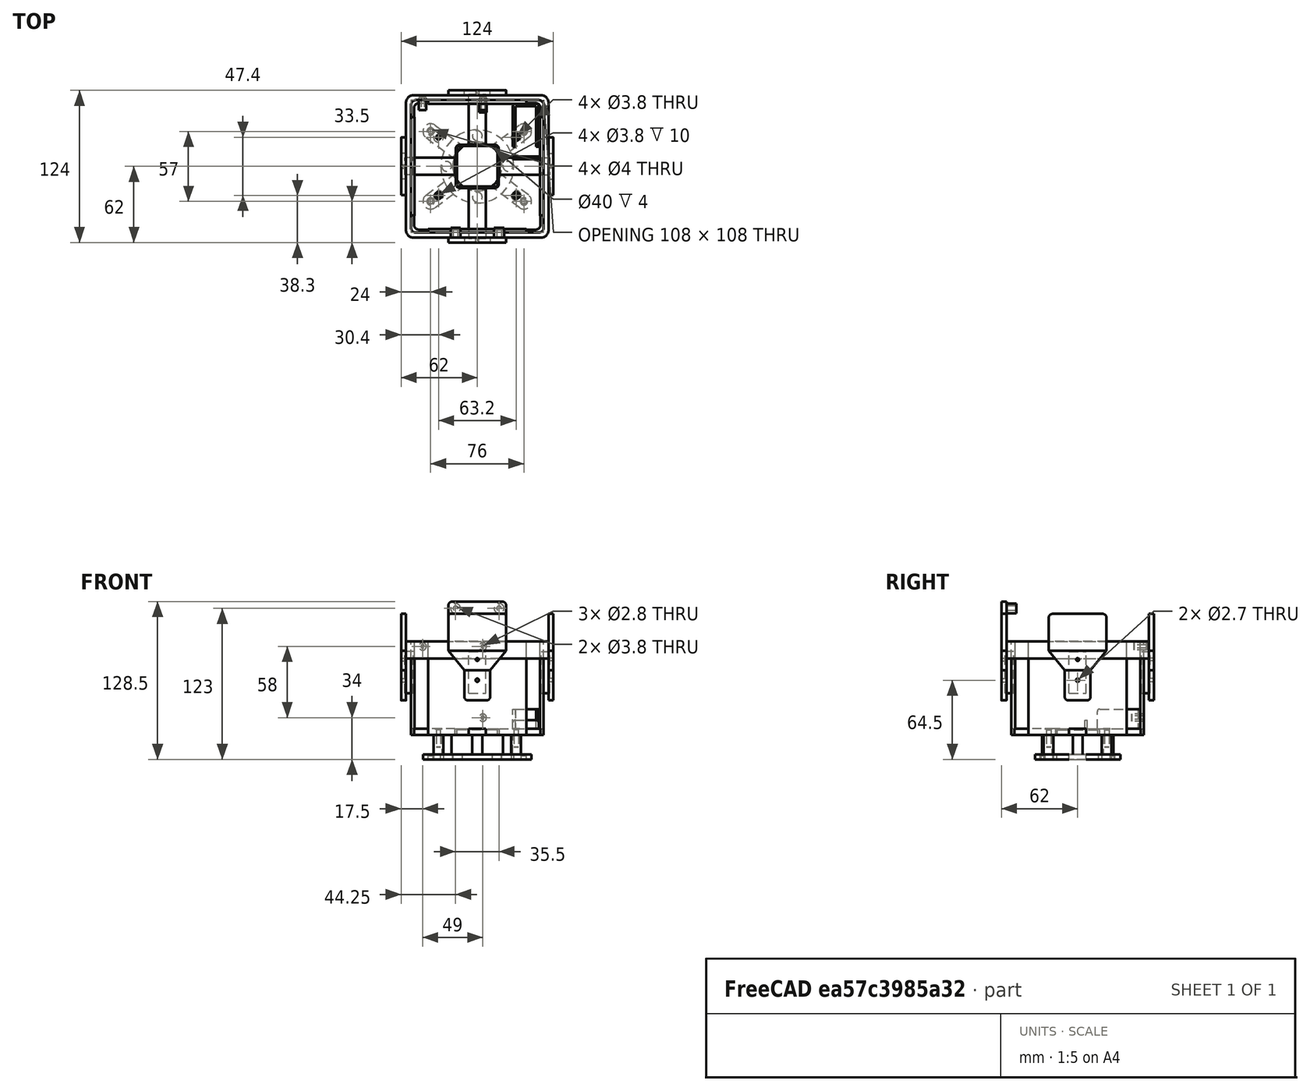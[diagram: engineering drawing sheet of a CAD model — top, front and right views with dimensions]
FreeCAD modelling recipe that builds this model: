
FCSTD DOCUMENT  (FreeCAD 0.20R)
Label: wAP60G multisupport robomaster rev02_1
License: All rights reserved
LicenseURL: http://en.wikipedia.org/wiki/All_rights_reserved
objects: Part::Box×16, Part::Cylinder×13, Part::FeaturePython×13, Part::Fillet×11, Part::Compound×6, Part::Cut×5, Part::MultiFuse×2, Part::Chamfer×2, App::LinkGroup×2, PartDesign::AdditiveWedge×1, PartDesign::Body×1, Part::Fuse×1
note: 72 computed .brp shape members not serialized (recipe doc carries the construction recipe); baked Part::Feature solids carry a one-line shape summary decoded from their .brp

FEATURE [Part::Box] Box  label="Cubo"
  AttacherType = Attacher::AttachEngine3D
  Height = 24.5
  Length = 21
  Placement = pos=(-10.5,0,0) rot=(0,0,1;0rad)
  Width = 4
  expr: .Placement.Base.x = -Length / 2
FEATURE [PartDesign::AdditiveWedge] Wedge
  AttacherType = Attacher::AttachEngine3D
  X2max = 23.5
  X2min = -23.5
  Xmax = 10.5
  Xmin = -10.5
  Ymax = 16
  Ymin = 0
  Z2max = 4
  Z2min = 0
  Zmax = 4
  Zmin = 0
  expr: Xmax = <<Cubo>>.Length / 2
  expr: Xmin = -<<Cubo>>.Length / 2
  expr: Z2max = <<Cubo>>.Width
  expr: Zmax = <<Cubo>>.Width
FEATURE [PartDesign::Body] Body
  Group = -> [Wedge]
  Origin = -> Origin
  Placement = pos=(0,4,24.5) rot=(1,0,0;1.5708rad)
  Tip = -> Wedge
  expr: .Placement.Base.y = <<Cubo>>.Width
  expr: .Placement.Base.z = <<Cubo>>.Height
FEATURE [Part::Box] Box001  label="Cubo001"
  AttacherType = Attacher::AttachEngine3D
  Height = 30
  Length = 47
  Placement = pos=(-23.5,0,20.5) rot=(0,0,1;0rad)
  Width = 4
  expr: .Placement.Base.x = <<Wedge>>.X2min
  expr: .Placement.Base.z = <<Cubo>>.Height + <<Wedge>>.Ymax - 20mm
  expr: Length = <<Wedge>>.X2max - <<Wedge>>.X2min
  expr: Width = <<Cubo>>.Width
FEATURE [Part::Cylinder] Cylinder  label="Cilindro"
  Angle = 360
  AttacherType = Attacher::AttachEngine3D
  FirstAngle = 0
  Height = 4
  Placement = pos=(0,4,16.5) rot=(1,0,0;1.5708rad)
  Radius = 1.35
  SecondAngle = 0
  expr: .Placement.Base.y = <<Cubo>>.Width
  expr: Height = <<Cubo>>.Width
  expr: Radius = 2.7 / 2
FEATURE [Part::Cylinder] Cylinder001  label="Cilindro001"
  Angle = 360
  AttacherType = Attacher::AttachEngine3D
  FirstAngle = 0
  Height = 4
  Placement = pos=(0,4,33.3) rot=(1,0,0;1.5708rad)
  Radius = 1.2
  SecondAngle = 0
  expr: .Placement.Base.y = <<Cubo>>.Width
  expr: Height = <<Cubo>>.Width
  expr: Radius = 2.4 / 2
FEATURE [Part::FeaturePython] Cutout  # WARN: FeaturePython — macro-defined, semantics opaque (R4)
  Base = -> Box
  Placement = pos=(0,0,-20) rot=(0,0,1;0rad)
  Tolerance = 0
  Tool = -> Cylinder
FEATURE [Part::FeaturePython] Cutout001  # WARN: FeaturePython — macro-defined, semantics opaque (R4)
  Base = -> Body
  Placement = pos=(0,0,-20) rot=(0,0,1;0rad)
  Tolerance = 0
  Tool = -> Cylinder001
FEATURE [Part::Box] Box002  label="Cubo002"
  AttacherType = Attacher::AttachEngine3D
  Height = 14
  Length = 116
  Placement = pos=(-58,-4,14) rot=(0,0,1;0rad)
  Width = 4
  expr: .Placement.Base.x = -Length / 2
  expr: .Placement.Base.y = -Width
FEATURE [Part::Box] Box004  label="Cubo004"
  AttacherType = Attacher::AttachEngine3D
  Height = 3
  Length = 80
  Placement = pos=(-40,-4,-48) rot=(1,0,0;1.5708rad)
  Width = 76
  expr: .Placement.Base.x = -Length / 2
  expr: Height = 3
  expr: Length = 80
FEATURE [Part::Box] Box003  label="Cubo003"
  AttacherType = Attacher::AttachEngine3D
  Height = 5
  Length = 14
  Placement = pos=(-7,-40,-48) rot=(0,0,1;0rad)
  Width = 36
  expr: .Placement.Base.x = -Length / 2
FEATURE [Part::Box] Box006  label="Arm001"
  AttacherType = Attacher::AttachEngine3D
  Height = 4
  Length = 27.5
  Placement = pos=(-47.5,-6.25,0) rot=(0,0,1;0rad)
  Width = 12.5
  expr: .Placement.Base.x = <<ToeOuter001>>.Placement.Base.x
  expr: .Placement.Base.y = -<<ToeOuter001>>.OuterRadius
  expr: Height = <<Trunk>>.Height
  expr: Length = abs(<<ToeOuter001>>.Placement.Base.x) - <<Trunk>>.InnerRadius
  expr: Width = 2 * <<ToeOuter001>>.OuterRadius
FEATURE [Part::Cylinder] Cylinder002  label="SpacerOuter001"
  Angle = 360
  AttacherType = Attacher::AttachEngine3D
  FirstAngle = 0
  Height = 20
  Placement = pos=(-39.5,0,0) rot=(0,0,1;0rad)
  Radius = 4
  SecondAngle = 0
  expr: .Placement.Base.x = <<ToeOuter001>>.Placement.Base.x + <<ToeInner001>>.Radius + Radius + 2mm
FEATURE [Part::Cylinder] Cylinder003  label="SpacerInner001"
  Angle = 360
  AttacherType = Attacher::AttachEngine3D
  FirstAngle = 0
  Height = 10
  Placement = pos=(-39.5,0,10) rot=(0,0,1;0rad)
  Radius = 1.9
  SecondAngle = 0
  expr: .Placement.Base.x = <<SpacerOuter001>>.Placement.Base.x
  expr: .Placement.Base.z = <<SpacerOuter001>>.Height - Height
  expr: Radius = 3.8 / 2
FEATURE [Part::Cylinder] Cylinder004  label="ToeInner001"
  Angle = 360
  AttacherType = Attacher::AttachEngine3D
  FirstAngle = 0
  Height = 4
  Placement = pos=(-47.5,0,0) rot=(0,0,1;0rad)
  Radius = 2
  SecondAngle = 0
  expr: .Placement.Base = <<ToeOuter001>>.Placement.Base
  expr: Height = <<Trunk>>.Height
  expr: Radius = 4 / 2
FEATURE [Part::Cut] Cut  label="Spacer001"
  Base = -> Cylinder002
  Tool = -> Cylinder003
FEATURE [Part::FeaturePython] Tube  label="Trunk"  # WARN: FeaturePython — macro-defined, semantics opaque (R4)
  AttacherType = Attacher::AttachEngine3D
  Height = 4
  InnerRadius = 20
  OuterRadius = 29.75
FEATURE [Part::FeaturePython] Tube001  label="ToeOuter001"  # WARN: FeaturePython — macro-defined, semantics opaque (R4)
  AttacherType = Attacher::AttachEngine3D
  Height = 4
  InnerRadius = 0
  OuterRadius = 6.25
  Placement = pos=(-47.5,0,0) rot=(0,0,1;0rad)
  expr: Height = <<Trunk>>.Height
  expr: InnerRadius = 0
FEATURE [Part::MultiFuse] Fusion001  label="ArmToe001"
  Shapes = -> [Tube001,Box006]
FEATURE [Part::Cut] Cut001  label="Finger001"
  Base = -> Fusion001
  Tool = -> Cylinder004
FEATURE [Part::Chamfer] Chamfer
  Base = -> Cut001
  Edges = 3 edges r=1: [Edge10,Edge11,Edge12]
FEATURE [Part::Compound] Compound001  label="Foot001"
  Links = -> [Cut,Chamfer]
  Placement = pos=(0,0,0) rot=(0,0,1;0.643501rad)
  expr: .Placement.Rotation.Angle = asin(57 / 2 / (-<<ToeOuter001>>.Placement.Base.x / 1mm))
FEATURE [Part::FeaturePython] Clone  label="Foot002"  # Draft clone (typed FeaturePython)
  AttacherType = Attacher::AttachEngine3D
  Fuse = false
  Objects = -> [Compound001]
  Placement = pos=(0,0,0) rot=(0,0,-1;0.643501rad)
  Scale = (1,1,1)
  expr: .Placement.Rotation.Angle = asin(57 / 2 / (-<<ToeOuter001>>.Placement.Base.x / 1mm))
FEATURE [Part::FeaturePython] Clone001  label="Foot003"  # Draft clone (typed FeaturePython)
  AttacherType = Attacher::AttachEngine3D
  Fuse = false
  Objects = -> [Compound001]
  Placement = pos=(0,0,0) rot=(0,0,1;3.78509rad)
  Scale = (1,1,1)
  expr: .Placement.Rotation.Angle = 180° + asin(57 / 2 / (-<<ToeOuter001>>.Placement.Base.x / 1mm))
FEATURE [Part::FeaturePython] Clone002  label="Foot004"  # Draft clone (typed FeaturePython)
  AttacherType = Attacher::AttachEngine3D
  Fuse = false
  Objects = -> [Compound001]
  Placement = pos=(0,0,0) rot=(0,0,1;2.49809rad)
  Scale = (1,1,1)
  expr: .Placement.Rotation.Angle = 180° - asin(57 / 2 / (-<<ToeOuter001>>.Placement.Base.x / 1mm))
FEATURE [Part::Compound] Compound002
  Links = -> [Tube,Compound001,Clone,Clone001,Clone002]
  Placement = pos=(0,0,-68) rot=(0,0,1;0rad)
FEATURE [Part::Box] Box007  label="Cubo006"
  AttacherType = Attacher::AttachEngine3D
  Height = 34
  Length = 14
  Placement = pos=(-7,-6,-14) rot=(0,0,1;0rad)
  Width = 7
  expr: .Placement.Base.x = -Length / 2
  expr: Length = <<Cubo003>>.Length
FEATURE [Part::Compound] Compound  label="Compound001"
  Links = -> [Box001,Cutout,Cutout001,Box002,Box003,Box004,Box007]
  Placement = pos=(0,58,0) rot=(0,0,1;0rad)
FEATURE [Part::FeaturePython] Array  # Draft array (typed FeaturePython)
  Angle = 360
  ArrayType = 1
  Axis = (0,0,1)
  Base = -> Compound
  Center = (0,0,0)
  Fuse = true
  IntervalAxis = (0,0,0)
  IntervalX = (50,0,0)
  IntervalY = (0,50,0)
  IntervalZ = (0,0,50)
  NumberCircles = 3
  NumberPolar = 4
  NumberX = 2
  NumberY = 2
  NumberZ = 1
  RadialDistance = 50
  Symmetry = 1
  TangentialDistance = 25
FEATURE [Part::Box] Box009  label="Cubo008"
  AttacherType = Attacher::AttachEngine3D
  Height = 5
  Length = 33
  Placement = pos=(-16.5,-16.5,-48) rot=(0,0,1;0rad)
  Width = 33
  expr: .Placement.Base.x = -Length / 2
  expr: .Placement.Base.y = -Width / 2
  expr: .Placement.Base.z = <<Cubo003>>.Placement.Base.z
  expr: Height = <<Cubo003>>.Height
  expr: Length = <<Cubo009>>.Length - 39mm
  expr: Width = Length
FEATURE [Part::Box] Box010  label="Cubo009"
  AttacherType = Attacher::AttachEngine3D
  Height = 5
  Length = 72
  Placement = pos=(-36,-36,-48) rot=(0,0,1;0rad)
  Width = 72
  expr: .Placement.Base.x = -Length / 2
  expr: .Placement.Base.y = -Width / 2
  expr: .Placement.Base.z = <<Cubo003>>.Placement.Base.z
  expr: Height = <<Cubo003>>.Height
  expr: Width = Length
FEATURE [Part::Cut] Cut003
  Base = -> Box010
  Tool = -> Box009
FEATURE [Part::Fillet] Fillet002
  Base = -> Cut003
  Edges = 4 edges r=2: [Edge21,Edge22,Edge23,Edge24]
FEATURE [Part::Fillet] Fillet003
  Base = -> Fillet002
  Edges = 4 edges r=4: [Edge29,Edge30,Edge33,Edge35]
FEATURE [Part::Cylinder] Cylinder005  label="Cilindro002"
  Angle = 360
  AttacherType = Attacher::AttachEngine3D
  FirstAngle = 0
  Height = 5
  Placement = pos=(31.6,-23.7,-48) rot=(0,0,1;0rad)
  Radius = 1.9
  SecondAngle = 0
  expr: .Placement.Base.z = <<Cubo003>>.Placement.Base.z
FEATURE [Part::Cylinder] Cylinder006  label="Cilindro003"
  Angle = 360
  AttacherType = Attacher::AttachEngine3D
  FirstAngle = 0
  Height = 5
  Placement = pos=(31.6,23.7,-48) rot=(0,0,1;0rad)
  Radius = 1.9
  SecondAngle = 0
  expr: .Placement.Base.x = <<Cilindro002>>.Placement.Base.x
  expr: .Placement.Base.y = -<<Cilindro002>>.Placement.Base.y
  expr: .Placement.Base.z = <<Cilindro002>>.Placement.Base.z
  expr: Height = <<Cilindro002>>.Height
  expr: Radius = <<Cilindro002>>.Radius
FEATURE [Part::Cylinder] Cylinder007  label="Cilindro004"
  Angle = 360
  AttacherType = Attacher::AttachEngine3D
  FirstAngle = 0
  Height = 5
  Placement = pos=(-31.6,23.7,-48) rot=(0,0,1;0rad)
  Radius = 1.9
  SecondAngle = 0
  expr: .Placement.Base.x = -<<Cilindro002>>.Placement.Base.x
  expr: .Placement.Base.y = -<<Cilindro002>>.Placement.Base.y
  expr: .Placement.Base.z = <<Cilindro002>>.Placement.Base.z
  expr: Height = <<Cilindro002>>.Height
  expr: Radius = <<Cilindro002>>.Radius
FEATURE [Part::Cylinder] Cylinder008  label="Cilindro005"
  Angle = 360
  AttacherType = Attacher::AttachEngine3D
  FirstAngle = 0
  Height = 5
  Placement = pos=(-31.6,-23.7,-48) rot=(0,0,1;0rad)
  Radius = 1.9
  SecondAngle = 0
  expr: .Placement.Base.x = -<<Cilindro002>>.Placement.Base.x
  expr: .Placement.Base.y = <<Cilindro002>>.Placement.Base.y
  expr: .Placement.Base.z = <<Cilindro002>>.Placement.Base.z
  expr: Height = <<Cilindro002>>.Height
  expr: Radius = <<Cilindro002>>.Radius
FEATURE [Part::Compound] Compound003
  Links = -> [Cylinder005,Cylinder006,Cylinder007,Cylinder008]
FEATURE [Part::FeaturePython] Tube002  # WARN: FeaturePython — macro-defined, semantics opaque (R4)
  AttacherType = Attacher::AttachEngine3D
  Height = 10
  InnerRadius = 1.4
  OuterRadius = 3
  Placement = pos=(-24.5,56,24) rot=(1,0,0;1.5708rad)
  expr: InnerRadius = 2.8 / 2
FEATURE [Part::FeaturePython] Tube003  # WARN: FeaturePython — macro-defined, semantics opaque (R4)
  AttacherType = Attacher::AttachEngine3D
  Height = 10
  InnerRadius = 1.4
  OuterRadius = 3
  Placement = pos=(24.5,56,24) rot=(1,0,0;1.5708rad)
  expr: .Placement.Base.x = -<<Tube002>>.Placement.Base.x
  expr: .Placement.Base.y = <<Tube002>>.Placement.Base.y
  expr: .Placement.Base.z = <<Tube002>>.Placement.Base.z
  expr: Height = <<Tube002>>.Height
  expr: InnerRadius = 2.8 / 2
FEATURE [Part::FeaturePython] Tube004  # WARN: FeaturePython — macro-defined, semantics opaque (R4)
  AttacherType = Attacher::AttachEngine3D
  Height = 8
  InnerRadius = 1.9
  OuterRadius = 4
  Placement = pos=(-17.75,-50,55) rot=(1,0,0;1.5708rad)
  expr: .Placement.Base.x = -35.5 / 2
  expr: InnerRadius = 3.8 / 2
FEATURE [Part::Compound] Compound004
  Links = -> [Tube002,Tube003]
  Placement = pos=(-20,0,0) rot=(0,0,1;0rad)
FEATURE [Part::FeaturePython] Tube005  # WARN: FeaturePython — macro-defined, semantics opaque (R4)
  AttacherType = Attacher::AttachEngine3D
  Height = 8
  InnerRadius = 1.9
  OuterRadius = 4
  Placement = pos=(17.75,-50,55) rot=(1,0,0;1.5708rad)
  expr: .Placement.Base.x = -Tube004.Placement.Base.x
  expr: .Placement.Base.y = Tube004.Placement.Base.y
  expr: .Placement.Base.z = Tube004.Placement.Base.z
  expr: Height = Tube004.Height
  expr: InnerRadius = 3.8 / 2
  expr: OuterRadius = <<Tube004>>.OuterRadius
FEATURE [Part::Compound] Compound005
  Links = -> [Tube004,Tube005]
FEATURE [Part::Box] Box011  label="Cubo010"
  AttacherType = Attacher::AttachEngine3D
  Height = 10
  Length = 47
  Placement = pos=(-23.5,-62,50.5) rot=(0,0,1;0rad)
  Width = 4
  expr: .Placement.Base.x = <<Wedge>>.X2min
  expr: .Placement.Base.z = <<Cubo>>.Height + <<Wedge>>.Ymax + <<Cubo001>>.Height - 20mm
  expr: Width = <<Cubo>>.Width
FEATURE [Part::Box] Box012  label="Cubo011"
  AttacherType = Attacher::AttachEngine3D
  Height = 5
  Length = 103
  Placement = pos=(-51.5,-51.5,-48) rot=(0,0,1;0rad)
  Width = 103
  expr: .Placement.Base.x = -Length / 2
  expr: .Placement.Base.y = -Width / 2
  expr: .Placement.Base.z = <<Cubo003>>.Placement.Base.z
  expr: Height = <<Cubo003>>.Height
  expr: Width = Length
FEATURE [Part::Box] Box013  label="Cubo012"
  AttacherType = Attacher::AttachEngine3D
  Height = 5
  Length = 69.4
  Placement = pos=(-34.7,-34.7,-48) rot=(0,0,1;0rad)
  Width = 69.4
  expr: .Placement.Base.x = -Length / 2
  expr: .Placement.Base.y = -Width / 2
  expr: .Placement.Base.z = <<Cubo003>>.Placement.Base.z
  expr: Height = <<Cubo003>>.Height
  expr: Length = <<Cubo011>>.Length - 33.6mm
  expr: Width = Length
FEATURE [Part::Cut] Cut005
  Base = -> Box012
  Tool = -> Box013
FEATURE [Part::Fillet] Fillet005
  Base = -> Cut005
  Edges = 4 edges r=4: [Edge1,Edge3,Edge6,Edge15]
FEATURE [Part::Fillet] Fillet006
  Base = -> Fillet005
  Edges = 4 edges r=2: [Edge33,Edge34,Edge35,Edge36]
FEATURE [Part::Fillet] Fillet007
  Base = -> Array
  Edges = 4 edges r=6: [Edge1,Edge3,Edge20,Edge24]
FEATURE [Part::Fillet] Fillet008
  Base = -> Fillet007
  Edges = 4 edges r=4: [Edge33,Edge34,Edge35,Edge36]
FEATURE [Part::Fillet] Fillet009
  Base = -> Fillet008
  Edges = 4 edges r=1: [Edge114,Edge192,Edge270,Edge348]
FEATURE [Part::Fillet] Fillet010
  Base = -> Box011
  Edges = 2 edges r=3: [Edge2,Edge6]
FEATURE [Part::Fillet] Fillet011
  Base = -> Fillet009
  Edges = 14 edges r=3: [Edge110,Edge114,Edge124,Edge134,Edge176,Edge180,Edge190,Edge200,Edge256,Edge266,Edge308,Edge312,Edge322,Edge332]
FEATURE [Part::Cut] Cut006
  Base = -> Fillet003
  Tool = -> Compound003
FEATURE [Part::Chamfer] Chamfer001
  Base = -> Cut006
  Edges = 4 edges r=1: [Edge9,Edge10,Edge11,Edge20]
FEATURE [Part::Box] Box014  label="Cubo013"
  AttacherType = Attacher::AttachEngine3D
  Height = 16
  Length = 2
  Placement = pos=(29,29,-46) rot=(0,0,1;0rad)
  Width = 35
FEATURE [Part::Box] Box015  label="Cubo014"
  AttacherType = Attacher::AttachEngine3D
  Height = 16
  Length = 2
  Placement = pos=(48,29,-46) rot=(0,0,1;0rad)
  Width = 35
  expr: .Placement.Base.x = <<Cubo013>>.Placement.Base.x + 17mm + <<Cubo013>>.Length
  expr: .Placement.Base.y = <<Cubo013>>.Placement.Base.y
  expr: .Placement.Base.z = <<Cubo013>>.Placement.Base.z
  expr: Height = <<Cubo013>>.Height
  expr: Length = <<Cubo013>>.Length
  expr: Width = <<Cubo013>>.Width
FEATURE [Part::Box] Box016  label="Cubo015"
  AttacherType = Attacher::AttachEngine3D
  Height = 7
  Length = 21
  Placement = pos=(29,12.5,-46) rot=(0,0,1;0rad)
  Width = 2
FEATURE [Part::Box] Box017  label="Cubo016"
  AttacherType = Attacher::AttachEngine3D
  Height = 16
  Length = 21
  Placement = pos=(29,62,-46) rot=(0,0,1;0rad)
  Width = 2
FEATURE [Part::MultiFuse] Fusion
  Refine = true
  Shapes = -> [Box017,Box014,Box015]
FEATURE [Part::Fillet] Fillet012
  Base = -> Fusion
  Edges = 4 edges r=2: [Edge3,Edge16,Edge17,Edge22]
  Placement = pos=(0,-13,3) rot=(0,0,1;0rad)
FEATURE [Part::Fillet] Fillet013
  Base = -> Box016
  Edges = 2 edges r=2: [Edge2,Edge6]
  Placement = pos=(0,-6.55,3) rot=(0,0,1;0rad)
FEATURE [Part::FeaturePython] Tube006  # WARN: FeaturePython — macro-defined, semantics opaque (R4)
  AttacherType = Attacher::AttachEngine3D
  Height = 10
  InnerRadius = 1.4
  OuterRadius = 3
  Placement = pos=(4.5,54,-34) rot=(1,0,0;1.5708rad)
  expr: InnerRadius = 2.8 / 2
FEATURE [Part::Fuse] Fusion002
  Base = -> Fillet006
  Refine = true
  Tool = -> Chamfer001
FEATURE [Part::Cylinder] Cylinder009  label="Cilindro006"
  Angle = 360
  AttacherType = Attacher::AttachEngine3D
  FirstAngle = 0
  Height = 16
  Placement = pos=(25,0,-64) rot=(0,0,1;0rad)
  Radius = 4
  SecondAngle = 0
FEATURE [Part::Cylinder] Cylinder010  label="Cilindro007"
  Angle = 360
  AttacherType = Attacher::AttachEngine3D
  FirstAngle = 0
  Height = 16
  Placement = pos=(-25,0,-64) rot=(0,0,1;0rad)
  Radius = 4
  SecondAngle = 0
FEATURE [Part::Cylinder] Cylinder011  label="Cilindro008"
  Angle = 360
  AttacherType = Attacher::AttachEngine3D
  FirstAngle = 0
  Height = 16
  Placement = pos=(0,25,-64) rot=(0,0,1;0rad)
  Radius = 4
  SecondAngle = 0
FEATURE [Part::Cylinder] Cylinder012  label="Cilindro009"
  Angle = 360
  AttacherType = Attacher::AttachEngine3D
  FirstAngle = 0
  Height = 16
  Placement = pos=(0,-25,-64) rot=(0,0,1;0rad)
  Radius = 4
  SecondAngle = 0
FEATURE [App::LinkGroup] LinkGroup  label="Platform"
  ElementList = -> [Compound002,Cylinder009,Cylinder010,Cylinder011,Cylinder012]
  LinkMode = 0
FEATURE [App::LinkGroup] LinkGroup001  label="Turret"
  ElementList = -> [Fusion002,Compound004,Compound005,Fillet010,Fillet011,Fillet012,Fillet013,Tube006]
  LinkMode = 0
